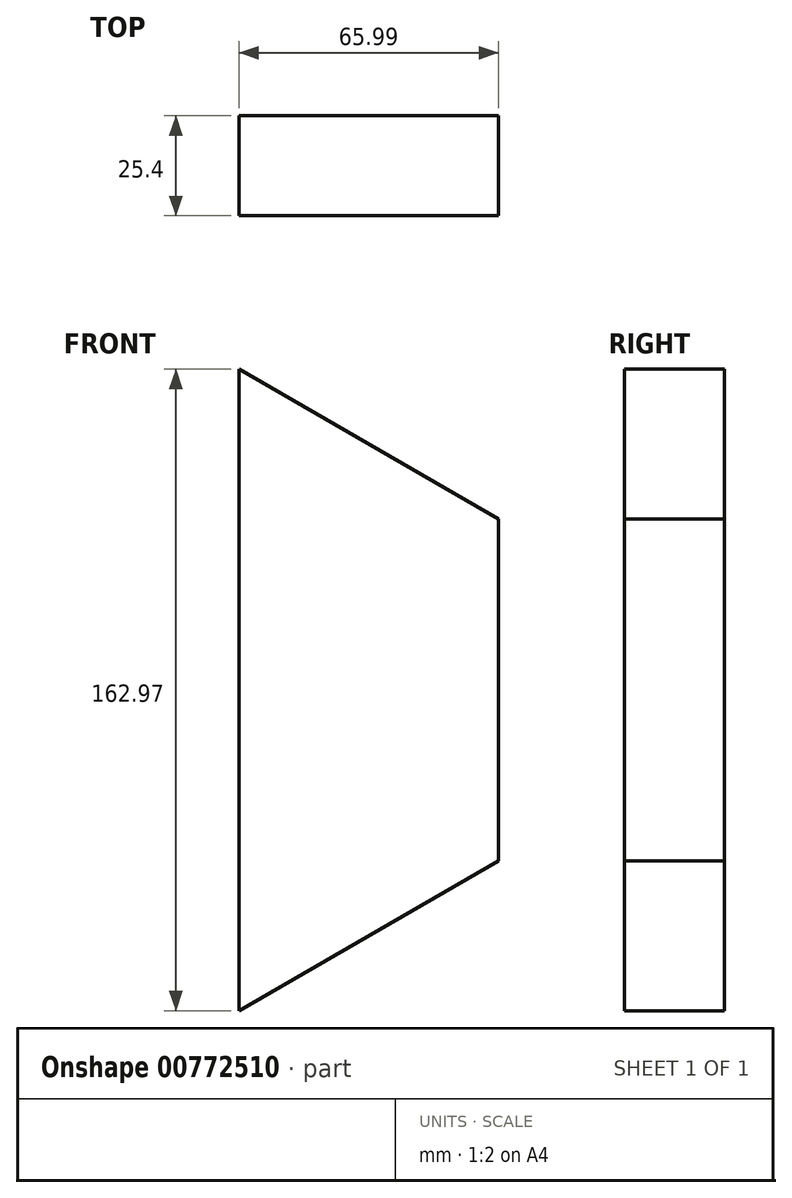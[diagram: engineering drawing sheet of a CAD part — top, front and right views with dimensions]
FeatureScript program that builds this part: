
annotation { "Feature Type Name" : "Feature", "Feature Type Description" : "" }
export const myFeature = defineFeature(function(context is Context, id is Id, definition is map)
    precondition{}
    {
        {
            var Q0;
            Q0=qCreatedBy(makeId("Front.planeOp"),FACE);
            var sketch = newSketch(context, id + "F0", { "sketchPlane" : qUnion([Q0])});
            skLineSegment(sketch, "E0", {"start": v(7.97, 45.01) * mm, "end": v(7.97, -41.76) * mm});
            skLineSegment(sketch, "E1", {"start": v(7.97, -41.76) * mm, "end": v(-58.02, -79.86) * mm});
            skLineSegment(sketch, "E2", {"start": v(-58.02, -79.86) * mm, "end": v(-58.02, 83.11) * mm});
            skLineSegment(sketch, "E3", {"start": v(-58.02, 83.11) * mm, "end": v(7.97, 45.01) * mm});
            skSolve(sketch);
        }
        {
            var Q0;
            Q0=makeQuery(id+"F0.imprint","IMPRINT",FACE,{"disambiguationData":[TD([[makeQuery(id+"F0.imprint","IMPRINT",EDGE,{"derivedFrom":sQuery(id+"F0.wireOp",EDGE,"E0")}),-1.0]])]});
            extrude(context, id + "F1", {"entities" : qUnion([Q0]), "depth" : 25.4 * mm, "offsetDistance" : 25.4 * mm});
        }
    });
